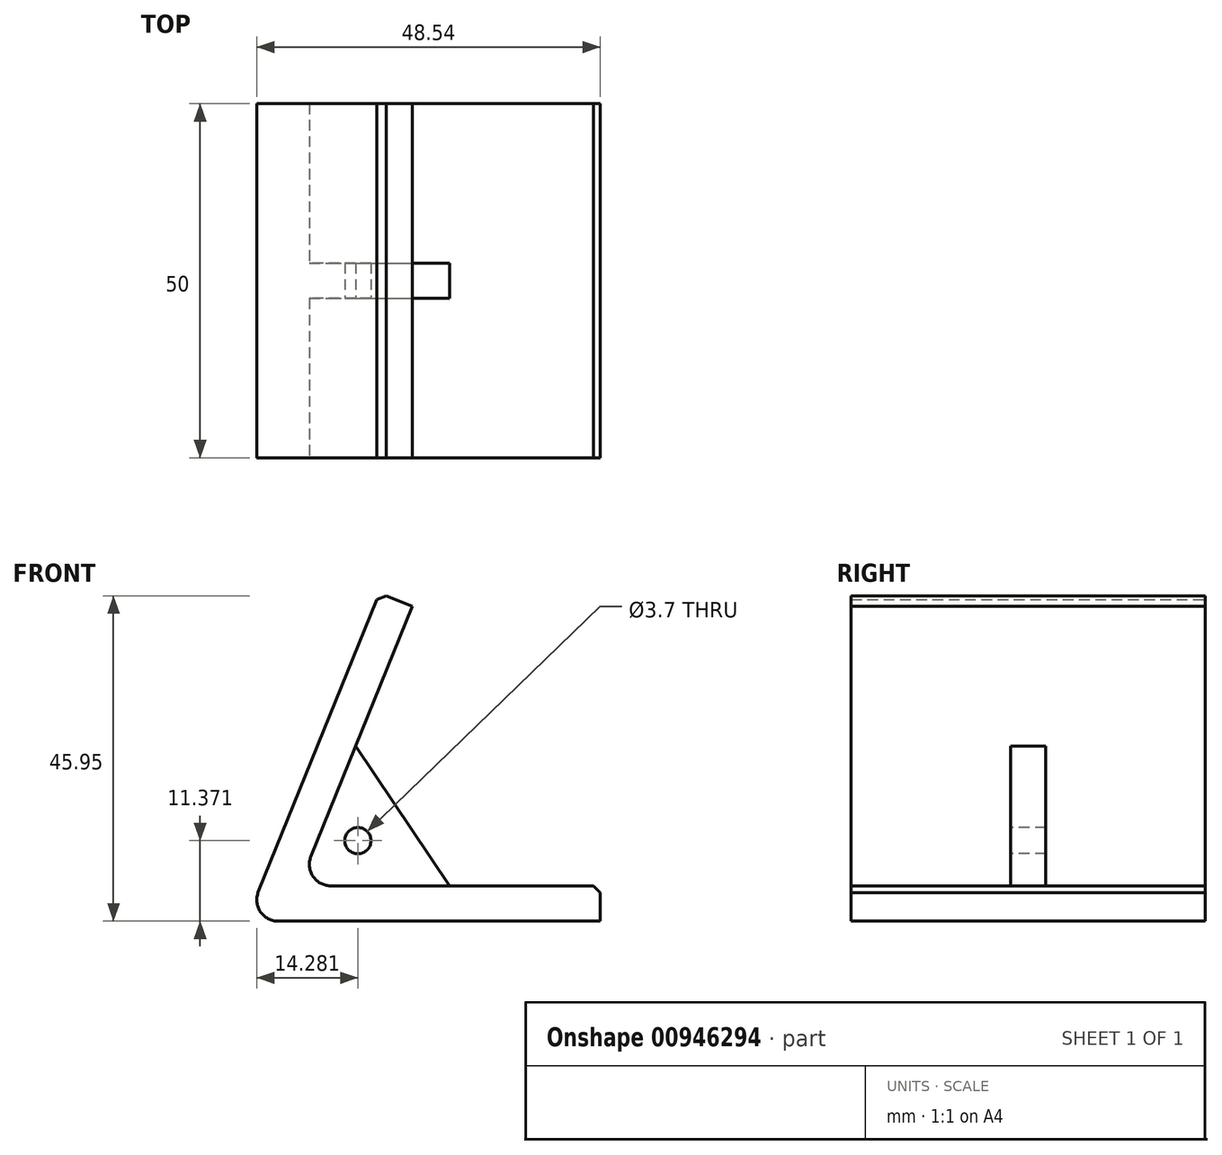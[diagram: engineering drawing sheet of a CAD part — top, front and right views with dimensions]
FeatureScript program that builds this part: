
annotation { "Feature Type Name" : "Feature", "Feature Type Description" : "" }
export const myFeature = defineFeature(function(context is Context, id is Id, definition is map)
    precondition{}
    {
        {
            var Q0;
            Q0=qCreatedBy(makeId("Front.planeOp"),FACE);
            var sketch = newSketch(context, id + "F0", { "sketchPlane" : qUnion([Q0])});
            skLineSegment(sketch, "E0", {"start": v(0, 0) * mm, "end": v(18.81, 46.33) * mm});
            skLineSegment(sketch, "E1", {"start": v(18.81, 46.33) * mm, "end": v(23.45, 44.44) * mm});
            skLineSegment(sketch, "E2", {"start": v(23.45, 44.44) * mm, "end": v(7.43, 5) * mm});
            skLineSegment(sketch, "E3", {"start": v(7.43, 5) * mm, "end": v(50, 5) * mm});
            skLineSegment(sketch, "E4", {"start": v(50, 5) * mm, "end": v(50, 0) * mm});
            skLineSegment(sketch, "E5", {"start": v(50, 0) * mm, "end": v(0, 0) * mm});
            skSolve(sketch);
        }
        {
            var Q0;
            Q0=makeQuery(id+"F0.imprint","IMPRINT",FACE,{"disambiguationData":[TD([[makeQuery(id+"F0.imprint","IMPRINT",EDGE,{"derivedFrom":sQuery(id+"F0.wireOp",EDGE,"E0")}),-1.0]])]});
            extrude(context, id + "F1", {"entities" : qUnion([Q0]), "depth" : 50 * mm, "offsetDistance" : 25 * mm});
        }
        {
            var Q0;
            Q0=qCreatedBy(makeId("Front.planeOp"),FACE);
            cPlane(context, id + "F2", {"entities" : qUnion([Q0]), "cplaneType" : CPlaneType.OFFSET, "offset" : 25 * mm, "width" : 150 * mm, "height" : 150 * mm});
        }
        {
            var Q0;
            Q0=qCreatedBy(id+"F2.planeOp",FACE);
            var sketch = newSketch(context, id + "F3", { "sketchPlane" : qUnion([Q0])});
            skLineSegment(sketch, "E6.0", {"start": v(15.44, 24.72) * mm, "end": v(7.43, 5) * mm});
            skLineSegment(sketch, "E7.0", {"start": v(7.43, 5) * mm, "end": v(28.71, 5) * mm});
            skLineSegment(sketch, "E8", {"start": v(15.44, 24.72) * mm, "end": v(28.71, 5) * mm});
            skPoint(sketch, "E9.orphan", {"position": v(23.45, 44.44) * mm});
            skPoint(sketch, "E10.orphan", {"position": v(50, 5) * mm});
            skCircle(sketch, "E11", {"center": v(15.74, 11.37) * mm, "radius": 1.85 * mm});
            skSolve(sketch);
        }
        {
            var Q0;
            Q0 = qSketchRegion(id + "F3", true);
            var Q1;
            Q1=makeQuery(id+"F1.opExtrude","CAP_FACE",FACE,{"disambiguationData":[OSD([sQuery(id+"F0.wireOp",EDGE,"E0"),sQuery(id+"F0.wireOp",EDGE,"E1"),sQuery(id+"F0.wireOp",EDGE,"E2"),sQuery(id+"F0.wireOp",EDGE,"E3"),sQuery(id+"F0.wireOp",EDGE,"E4"),sQuery(id+"F0.wireOp",EDGE,"E5")])],"isStart":true});
            var Q2;
            Q2=makeQuery(id+"F1.opExtrude","SWEPT_BODY",BODY,{"disambiguationData":[OSD([sQuery(id+"F0.wireOp",EDGE,"E0"),sQuery(id+"F0.wireOp",EDGE,"E1"),sQuery(id+"F0.wireOp",EDGE,"E2"),sQuery(id+"F0.wireOp",EDGE,"E3"),sQuery(id+"F0.wireOp",EDGE,"E4"),sQuery(id+"F0.wireOp",EDGE,"E5")])]});
            extrude(context, id + "F4", {"entities" : qUnion([Q0]), "operationType" : NewBodyOperationType.ADD, "oppositeDirection" : true, "depth" : 5 * mm, "endBoundEntityFace" : qUnion([Q1]), "endBoundEntityBody" : qUnion([Q2]), "offsetDistance" : 25 * mm, "symmetric" : true});
        }
        {
            var Q0;
            Q0=makeQuery(id+"F1.opExtrude","SWEPT_EDGE",EDGE,{"disambiguationData":[OSD([sQuery(id+"F0.wireOp",EDGE,"E0"),sQuery(id+"F0.wireOp",EDGE,"E5")])]});
            var Q1;
            Q1=makeQuery(id+"F4.opExtrude","CAP_EDGE",EDGE,{"disambiguationData":[OSD([sQuery(id+"F3.wireOp",EDGE,"E7.0")])],"isStart":true});
            var Q2;
            Q2=makeQuery(id+"F4.opExtrude","CAP_EDGE",EDGE,{"disambiguationData":[OSD([sQuery(id+"F3.wireOp",EDGE,"E6.0")])],"isStart":true});
            var Q3;
            Q3=makeQuery(id+"F4.opExtrude","CAP_EDGE",EDGE,{"disambiguationData":[OSD([sQuery(id+"F3.wireOp",EDGE,"E6.0")])],"isStart":false});
            var Q4;
            Q4=makeQuery(id+"F4.opExtrude","CAP_EDGE",EDGE,{"disambiguationData":[OSD([sQuery(id+"F3.wireOp",EDGE,"E7.0")])],"isStart":false});
            var Q5;
            {var subQ0=sQuery(id+"F0.wireOp",EDGE,"E3");var subQ1=sQuery(id+"F0.wireOp",EDGE,"E2");Q5=makeQuery(id+"F4.boolean.opBoolean","SPLIT",EDGE,{"disambiguationData":[TD([makeQuery(id+"F4.opExtrude","CAP_FACE",FACE,{"disambiguationData":[OSD([sQuery(id+"F3.wireOp",EDGE,"E6.0"),sQuery(id+"F3.wireOp",EDGE,"E7.0"),sQuery(id+"F3.wireOp",EDGE,"E8"),sQuery(id+"F3.wireOp",EDGE,"E11")])],"isStart":true})])],"derivedFrom":makeQuery(id+"F1.opExtrude","SWEPT_EDGE",EDGE,{"disambiguationData":[OSD([subQ1,subQ0])]})});}
            var Q6;
            {var subQ0=sQuery(id+"F0.wireOp",EDGE,"E3");var subQ1=sQuery(id+"F0.wireOp",EDGE,"E2");Q6=makeQuery(id+"F4.boolean.opBoolean","SPLIT",EDGE,{"disambiguationData":[TD([makeQuery(id+"F4.opExtrude","CAP_FACE",FACE,{"disambiguationData":[OSD([sQuery(id+"F3.wireOp",EDGE,"E6.0"),sQuery(id+"F3.wireOp",EDGE,"E7.0"),sQuery(id+"F3.wireOp",EDGE,"E8"),sQuery(id+"F3.wireOp",EDGE,"E11")])],"isStart":false})])],"derivedFrom":makeQuery(id+"F1.opExtrude","SWEPT_EDGE",EDGE,{"disambiguationData":[OSD([subQ1,subQ0])]})});}
            fillet(context, id + "F5", {"entities" : qUnion([Q0, Q1, Q2, Q3, Q4, Q5, Q6]), "radius" : 3 * mm, "tangentPropagation" : true, "allowEdgeOverflow" : false});
        }
        {
            var Q0;
            Q0=makeQuery(id+"F1.opExtrude","SWEPT_EDGE",EDGE,{"disambiguationData":[OSD([sQuery(id+"F0.wireOp",EDGE,"E0"),sQuery(id+"F0.wireOp",EDGE,"E1")])]});
            var Q1;
            Q1=makeQuery(id+"F1.opExtrude","SWEPT_EDGE",EDGE,{"disambiguationData":[OSD([sQuery(id+"F0.wireOp",EDGE,"E3"),sQuery(id+"F0.wireOp",EDGE,"E4")])]});
            chamfer(context, id + "F6", {"entities" : qUnion([Q0, Q1]), "width" : 1 * mm, "tangentPropagation" : true});
        }
    });
